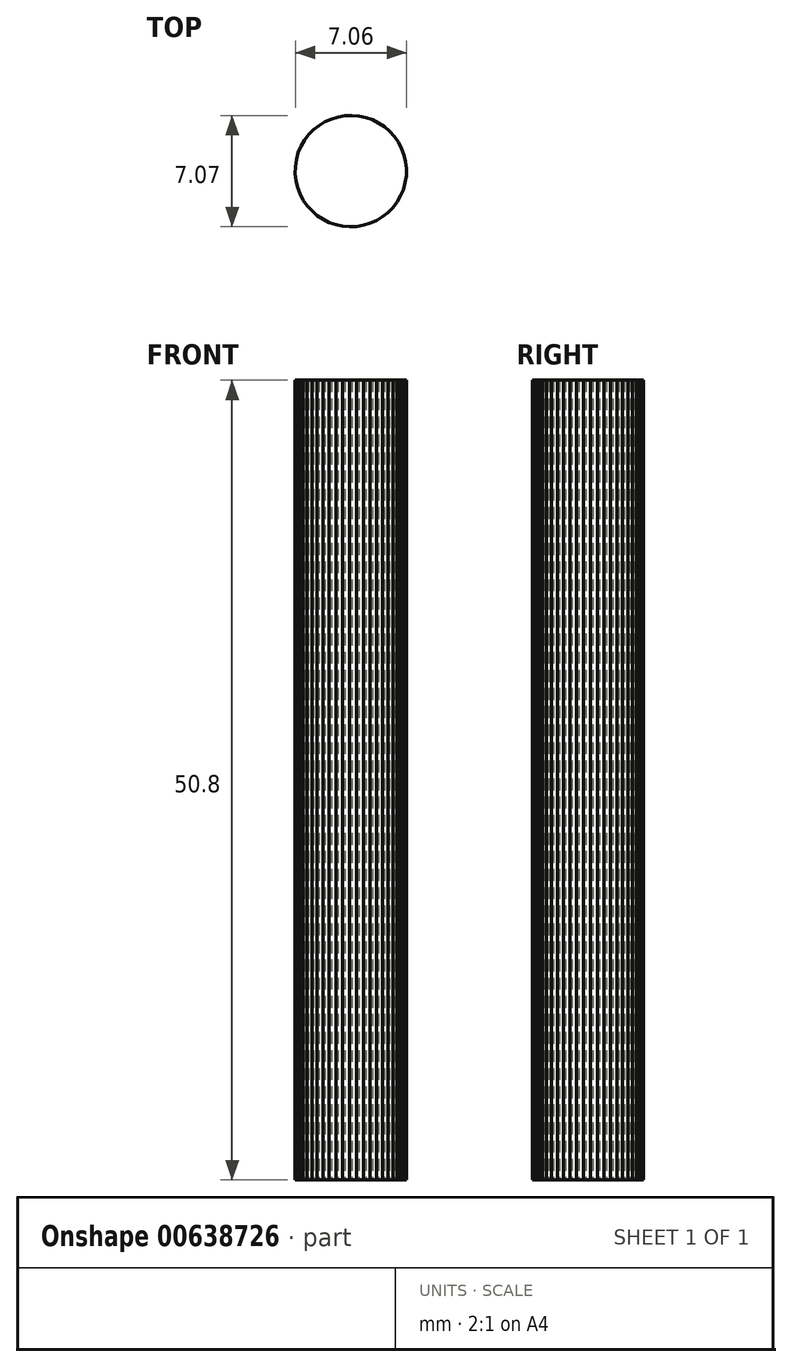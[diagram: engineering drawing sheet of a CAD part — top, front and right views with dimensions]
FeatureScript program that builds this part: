
annotation { "Feature Type Name" : "Feature", "Feature Type Description" : "" }
export const myFeature = defineFeature(function(context is Context, id is Id, definition is map)
    precondition{}
    {
        {
            var Q0;
            Q0=qCreatedBy(makeId("Top.planeOp"),FACE);
            var sketch = newSketch(context, id + "F0", { "sketchPlane" : qUnion([Q0])});
            skCircle(sketch, "E0.cCircle", {"center": v(0, 0) * mm, "radius": 62.4 * mm, "construction": true});
            skLineSegment(sketch, "E0.0", {"start": v(36.03, -62.4) * mm, "end": v(-36.03, -62.4) * mm});
            skLineSegment(sketch, "E0.1", {"start": v(-36.03, -62.4) * mm, "end": v(-72.06, 0) * mm});
            skLineSegment(sketch, "E0.2", {"start": v(-72.06, 0) * mm, "end": v(-36.03, 62.4) * mm});
            skLineSegment(sketch, "E0.3", {"start": v(-36.03, 62.4) * mm, "end": v(36.03, 62.4) * mm});
            skLineSegment(sketch, "E0.4", {"start": v(36.03, 62.4) * mm, "end": v(72.06, 0) * mm});
            skLineSegment(sketch, "E0.5", {"start": v(72.06, 0) * mm, "end": v(36.03, -62.4) * mm});
            skPoint(sketch, "E0.0.midPoint", {"position": v(0, -62.4) * mm});
            skCircle(sketch, "E1.cCircle", {"center": v(-109.56, -6.38) * mm, "radius": 3.53 * mm, "construction": true});
            skLineSegment(sketch, "E1.0", {"start": v(-106.4, -7.96) * mm, "end": v(-106.62, -8.34) * mm});
            skLineSegment(sketch, "E1.1", {"start": v(-106.62, -8.34) * mm, "end": v(-106.89, -8.7) * mm});
            skLineSegment(sketch, "E1.2", {"start": v(-106.89, -8.7) * mm, "end": v(-107.2, -9.01) * mm});
            skLineSegment(sketch, "E1.3", {"start": v(-107.2, -9.01) * mm, "end": v(-107.55, -9.29) * mm});
            skLineSegment(sketch, "E1.4", {"start": v(-107.55, -9.29) * mm, "end": v(-107.93, -9.52) * mm});
            skLineSegment(sketch, "E1.5", {"start": v(-107.93, -9.52) * mm, "end": v(-108.33, -9.7) * mm});
            skLineSegment(sketch, "E1.6", {"start": v(-108.33, -9.7) * mm, "end": v(-108.76, -9.82) * mm});
            skLineSegment(sketch, "E1.7", {"start": v(-108.76, -9.82) * mm, "end": v(-109.2, -9.9) * mm});
            skLineSegment(sketch, "E1.8", {"start": v(-109.2, -9.9) * mm, "end": v(-109.64, -9.92) * mm});
            skLineSegment(sketch, "E1.9", {"start": v(-109.64, -9.92) * mm, "end": v(-110.08, -9.88) * mm});
            skLineSegment(sketch, "E1.10", {"start": v(-110.08, -9.88) * mm, "end": v(-110.51, -9.79) * mm});
            skLineSegment(sketch, "E1.11", {"start": v(-110.51, -9.79) * mm, "end": v(-110.93, -9.64) * mm});
            skLineSegment(sketch, "E1.12", {"start": v(-110.93, -9.64) * mm, "end": v(-111.33, -9.44) * mm});
            skLineSegment(sketch, "E1.13", {"start": v(-111.33, -9.44) * mm, "end": v(-111.7, -9.2) * mm});
            skLineSegment(sketch, "E1.14", {"start": v(-111.7, -9.2) * mm, "end": v(-112.04, -8.9) * mm});
            skLineSegment(sketch, "E1.15", {"start": v(-112.04, -8.9) * mm, "end": v(-112.33, -8.58) * mm});
            skLineSegment(sketch, "E1.16", {"start": v(-112.33, -8.58) * mm, "end": v(-112.59, -8.21) * mm});
            skLineSegment(sketch, "E1.17", {"start": v(-112.59, -8.21) * mm, "end": v(-112.8, -7.82) * mm});
            skLineSegment(sketch, "E1.18", {"start": v(-112.8, -7.82) * mm, "end": v(-112.95, -7.4) * mm});
            skLineSegment(sketch, "E1.19", {"start": v(-112.95, -7.4) * mm, "end": v(-113.05, -6.97) * mm});
            skLineSegment(sketch, "E1.20", {"start": v(-113.05, -6.97) * mm, "end": v(-113.1, -6.53) * mm});
            skLineSegment(sketch, "E1.21", {"start": v(-113.1, -6.53) * mm, "end": v(-113.08, -6.09) * mm});
            skLineSegment(sketch, "E1.22", {"start": v(-113.08, -6.09) * mm, "end": v(-113.02, -5.65) * mm});
            skLineSegment(sketch, "E1.23", {"start": v(-113.02, -5.65) * mm, "end": v(-112.9, -5.22) * mm});
            skLineSegment(sketch, "E1.24", {"start": v(-112.9, -5.22) * mm, "end": v(-112.73, -4.81) * mm});
            skLineSegment(sketch, "E1.25", {"start": v(-112.73, -4.81) * mm, "end": v(-112.5, -4.43) * mm});
            skLineSegment(sketch, "E1.26", {"start": v(-112.5, -4.43) * mm, "end": v(-112.24, -4.08) * mm});
            skLineSegment(sketch, "E1.27", {"start": v(-112.24, -4.08) * mm, "end": v(-111.93, -3.76) * mm});
            skLineSegment(sketch, "E1.28", {"start": v(-111.93, -3.76) * mm, "end": v(-111.58, -3.48) * mm});
            skLineSegment(sketch, "E1.29", {"start": v(-111.58, -3.48) * mm, "end": v(-111.2, -3.25) * mm});
            skLineSegment(sketch, "E1.30", {"start": v(-111.2, -3.25) * mm, "end": v(-110.8, -3.07) * mm});
            skLineSegment(sketch, "E1.31", {"start": v(-110.8, -3.07) * mm, "end": v(-110.37, -2.94) * mm});
            skLineSegment(sketch, "E1.32", {"start": v(-110.37, -2.94) * mm, "end": v(-109.93, -2.87) * mm});
            skLineSegment(sketch, "E1.33", {"start": v(-109.93, -2.87) * mm, "end": v(-109.49, -2.85) * mm});
            skLineSegment(sketch, "E1.34", {"start": v(-109.49, -2.85) * mm, "end": v(-109.05, -2.89) * mm});
            skLineSegment(sketch, "E1.35", {"start": v(-109.05, -2.89) * mm, "end": v(-108.61, -2.98) * mm});
            skLineSegment(sketch, "E1.36", {"start": v(-108.61, -2.98) * mm, "end": v(-108.2, -3.13) * mm});
            skLineSegment(sketch, "E1.37", {"start": v(-108.2, -3.13) * mm, "end": v(-107.8, -3.32) * mm});
            skLineSegment(sketch, "E1.38", {"start": v(-107.8, -3.32) * mm, "end": v(-107.43, -3.57) * mm});
            skLineSegment(sketch, "E1.39", {"start": v(-107.43, -3.57) * mm, "end": v(-107.1, -3.86) * mm});
            skLineSegment(sketch, "E1.40", {"start": v(-107.1, -3.86) * mm, "end": v(-106.8, -4.19) * mm});
            skLineSegment(sketch, "E1.41", {"start": v(-106.8, -4.19) * mm, "end": v(-106.54, -4.55) * mm});
            skLineSegment(sketch, "E1.42", {"start": v(-106.54, -4.55) * mm, "end": v(-106.34, -4.95) * mm});
            skLineSegment(sketch, "E1.43", {"start": v(-106.34, -4.95) * mm, "end": v(-106.18, -5.36) * mm});
            skLineSegment(sketch, "E1.44", {"start": v(-106.18, -5.36) * mm, "end": v(-106.08, -5.8) * mm});
            skLineSegment(sketch, "E1.45", {"start": v(-106.08, -5.8) * mm, "end": v(-106.03, -6.24) * mm});
            skLineSegment(sketch, "E1.46", {"start": v(-106.03, -6.24) * mm, "end": v(-106.04, -6.68) * mm});
            skLineSegment(sketch, "E1.47", {"start": v(-106.04, -6.68) * mm, "end": v(-106.1, -7.12) * mm});
            skLineSegment(sketch, "E1.48", {"start": v(-106.1, -7.12) * mm, "end": v(-106.23, -7.55) * mm});
            skLineSegment(sketch, "E1.49", {"start": v(-106.23, -7.55) * mm, "end": v(-106.4, -7.96) * mm});
            skPoint(sketch, "E1.0.midPoint", {"position": v(-106.5, -8.15) * mm});
            skSolve(sketch);
        }
        {
            var Q0;
            Q0=makeQuery(id+"F0.imprint","IMPRINT",FACE,{"disambiguationData":[TD([[makeQuery(id+"F0.imprint","IMPRINT",EDGE,{"derivedFrom":sQuery(id+"F0.wireOp",EDGE,"E1.0")}),-1.0]])]});
            extrude(context, id + "F1", {"entities" : qUnion([Q0]), "depth" : 25.4 * mm, "offsetDistance" : 25.4 * mm});
        }
        {
            var Q0;
            Q0=makeQuery(id+"F1.opExtrude","CAP_FACE",FACE,{"disambiguationData":[OSD([sQuery(id+"F0.wireOp",EDGE,"E1.0"),sQuery(id+"F0.wireOp",EDGE,"E1.1"),sQuery(id+"F0.wireOp",EDGE,"E1.2"),sQuery(id+"F0.wireOp",EDGE,"E1.3"),sQuery(id+"F0.wireOp",EDGE,"E1.4"),sQuery(id+"F0.wireOp",EDGE,"E1.5"),sQuery(id+"F0.wireOp",EDGE,"E1.6"),sQuery(id+"F0.wireOp",EDGE,"E1.7"),sQuery(id+"F0.wireOp",EDGE,"E1.8"),sQuery(id+"F0.wireOp",EDGE,"E1.9"),sQuery(id+"F0.wireOp",EDGE,"E1.10"),sQuery(id+"F0.wireOp",EDGE,"E1.11"),sQuery(id+"F0.wireOp",EDGE,"E1.12"),sQuery(id+"F0.wireOp",EDGE,"E1.13"),sQuery(id+"F0.wireOp",EDGE,"E1.14"),sQuery(id+"F0.wireOp",EDGE,"E1.15"),sQuery(id+"F0.wireOp",EDGE,"E1.16"),sQuery(id+"F0.wireOp",EDGE,"E1.17"),sQuery(id+"F0.wireOp",EDGE,"E1.18"),sQuery(id+"F0.wireOp",EDGE,"E1.19"),sQuery(id+"F0.wireOp",EDGE,"E1.20"),sQuery(id+"F0.wireOp",EDGE,"E1.21"),sQuery(id+"F0.wireOp",EDGE,"E1.22"),sQuery(id+"F0.wireOp",EDGE,"E1.23"),sQuery(id+"F0.wireOp",EDGE,"E1.24"),sQuery(id+"F0.wireOp",EDGE,"E1.25"),sQuery(id+"F0.wireOp",EDGE,"E1.26"),sQuery(id+"F0.wireOp",EDGE,"E1.27"),sQuery(id+"F0.wireOp",EDGE,"E1.28"),sQuery(id+"F0.wireOp",EDGE,"E1.29"),sQuery(id+"F0.wireOp",EDGE,"E1.30"),sQuery(id+"F0.wireOp",EDGE,"E1.31"),sQuery(id+"F0.wireOp",EDGE,"E1.32"),sQuery(id+"F0.wireOp",EDGE,"E1.33"),sQuery(id+"F0.wireOp",EDGE,"E1.34"),sQuery(id+"F0.wireOp",EDGE,"E1.35"),sQuery(id+"F0.wireOp",EDGE,"E1.36"),sQuery(id+"F0.wireOp",EDGE,"E1.37"),sQuery(id+"F0.wireOp",EDGE,"E1.38"),sQuery(id+"F0.wireOp",EDGE,"E1.39"),sQuery(id+"F0.wireOp",EDGE,"E1.40"),sQuery(id+"F0.wireOp",EDGE,"E1.41"),sQuery(id+"F0.wireOp",EDGE,"E1.42"),sQuery(id+"F0.wireOp",EDGE,"E1.43"),sQuery(id+"F0.wireOp",EDGE,"E1.44"),sQuery(id+"F0.wireOp",EDGE,"E1.45"),sQuery(id+"F0.wireOp",EDGE,"E1.46"),sQuery(id+"F0.wireOp",EDGE,"E1.47"),sQuery(id+"F0.wireOp",EDGE,"E1.48"),sQuery(id+"F0.wireOp",EDGE,"E1.49")])],"isStart":false});
            extrude(context, id + "F2", {"entities" : qUnion([Q0]), "operationType" : NewBodyOperationType.ADD, "depth" : 25.4 * mm, "offsetDistance" : 25.4 * mm});
        }
    });
